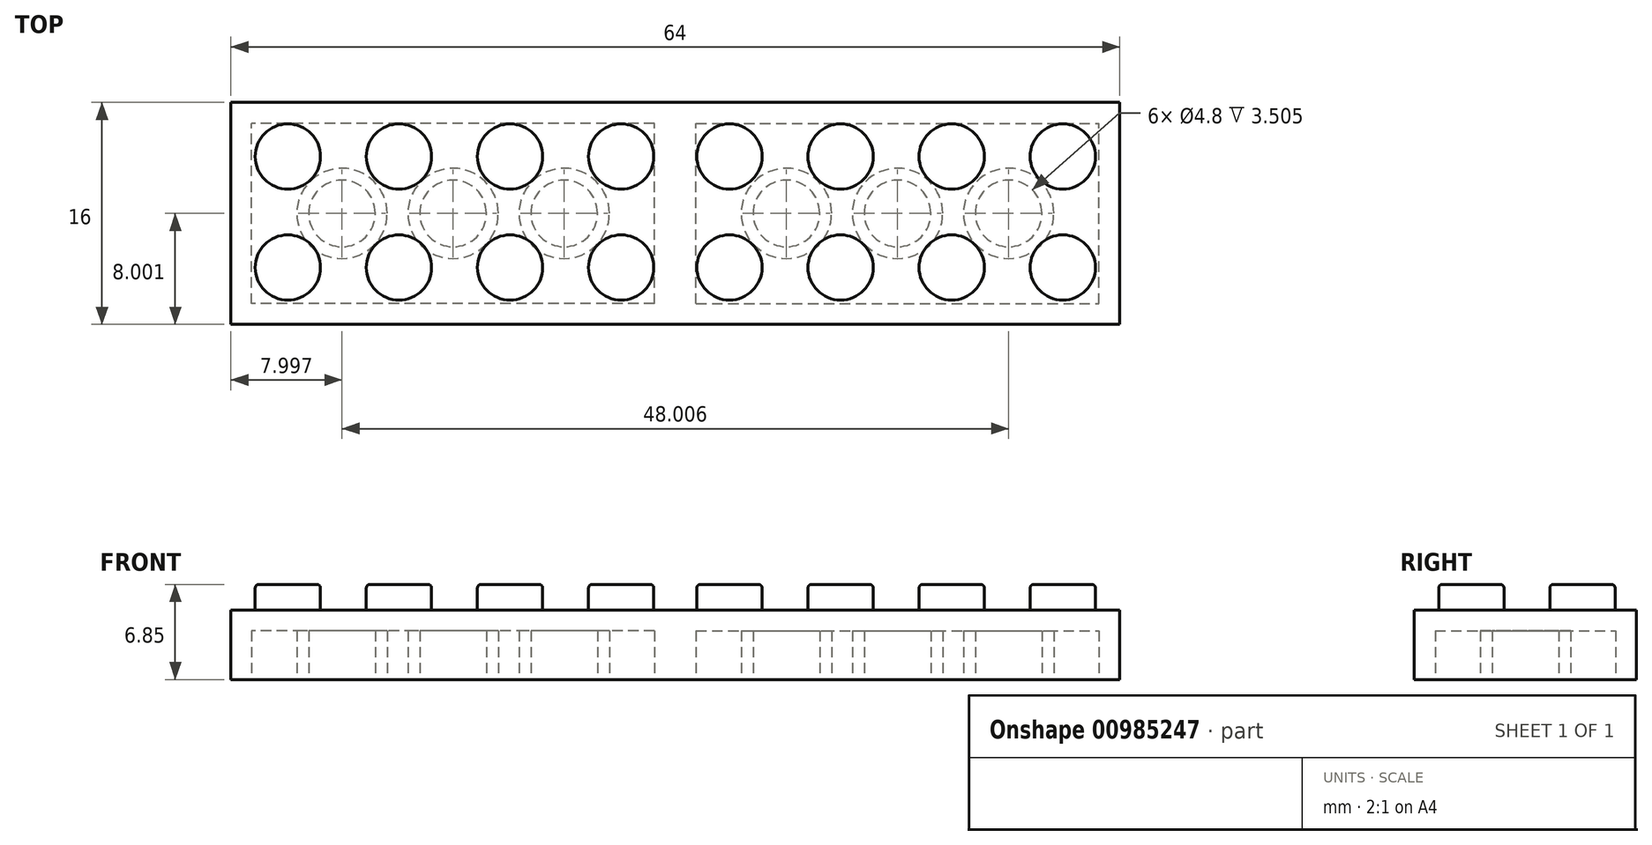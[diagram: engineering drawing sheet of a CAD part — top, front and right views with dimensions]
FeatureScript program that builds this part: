
annotation { "Feature Type Name" : "Feature", "Feature Type Description" : "" }
export const myFeature = defineFeature(function(context is Context, id is Id, definition is map)
    precondition{}
    {
        {
            var Q0;
            Q0=qCreatedBy(makeId("Top.planeOp"),FACE);
            var sketch = newSketch(context, id + "F0", { "sketchPlane" : qUnion([Q0])});
            skLineSegment(sketch, "E0.bottom", {"start": v(0, 0) * mm, "end": v(32, 0) * mm});
            skLineSegment(sketch, "E0.top", {"start": v(0, 16) * mm, "end": v(32, 16) * mm});
            skLineSegment(sketch, "E0.left", {"start": v(0, 0) * mm, "end": v(0, 16) * mm});
            skLineSegment(sketch, "E0.right", {"start": v(32, 0) * mm, "end": v(32, 16) * mm});
            skSolve(sketch);
        }
        {
            var Q0;
            Q0=makeQuery(id+"F0.imprint","IMPRINT",FACE,{"disambiguationData":[TD([[makeQuery(id+"F0.imprint","IMPRINT",EDGE,{"derivedFrom":sQuery(id+"F0.wireOp",EDGE,"E0.bottom")}),1.0]])]});
            extrude(context, id + "F1", {"entities" : qUnion([Q0]), "oppositeDirection" : true, "depth" : 5 * mm, "offsetDistance" : 25.4 * mm});
        }
        {
            var Q0;
            Q0=makeQuery(id+"F1.opExtrude","CAP_FACE",FACE,{"disambiguationData":[OSD([sQuery(id+"F0.wireOp",EDGE,"E0.bottom"),sQuery(id+"F0.wireOp",EDGE,"E0.top"),sQuery(id+"F0.wireOp",EDGE,"E0.left"),sQuery(id+"F0.wireOp",EDGE,"E0.right")])],"isStart":true});
            var sketch = newSketch(context, id + "F2", { "sketchPlane" : qUnion([Q0])});
            skCircle(sketch, "E1", {"center": v(3.9, 12.1) * mm, "radius": 2.35 * mm});
            skCircle(sketch, "E2.0.1.0", {"center": v(3.9, 4.1) * mm, "radius": 2.35 * mm});
            skCircle(sketch, "E2.1.0.0", {"center": v(11.9, 12.1) * mm, "radius": 2.35 * mm});
            skCircle(sketch, "E2.1.1.0", {"center": v(11.9, 4.1) * mm, "radius": 2.35 * mm});
            skCircle(sketch, "E2.2.0.0", {"center": v(19.9, 12.1) * mm, "radius": 2.35 * mm});
            skCircle(sketch, "E2.2.1.0", {"center": v(19.9, 4.1) * mm, "radius": 2.35 * mm});
            skCircle(sketch, "E2.3.0.0", {"center": v(27.9, 12.1) * mm, "radius": 2.35 * mm});
            skCircle(sketch, "E2.3.1.0", {"center": v(27.9, 4.1) * mm, "radius": 2.35 * mm});
            skLineSegment(sketch, "E2.direction1", {"start": v(3.9, 12.1) * mm, "end": v(11.9, 12.1) * mm, "construction": true});
            skLineSegment(sketch, "E2.direction2", {"start": v(3.9, 12.1) * mm, "end": v(3.9, 4.1) * mm, "construction": true});
            skSolve(sketch);
        }
        {
            var Q0;
            Q0=makeQuery(id+"F2.imprint","IMPRINT",FACE,{"disambiguationData":[TD([[makeQuery(id+"F2.imprint","IMPRINT",EDGE,{"derivedFrom":sQuery(id+"F2.wireOp",EDGE,"E1")}),1.0]])]});
            var Q1;
            Q1=makeQuery(id+"F2.imprint","IMPRINT",FACE,{"disambiguationData":[TD([[makeQuery(id+"F2.imprint","IMPRINT",EDGE,{"derivedFrom":sQuery(id+"F2.wireOp",EDGE,"E2.0.1.0")}),1.0]])]});
            var Q2;
            Q2=makeQuery(id+"F2.imprint","IMPRINT",FACE,{"disambiguationData":[TD([[makeQuery(id+"F2.imprint","IMPRINT",EDGE,{"derivedFrom":sQuery(id+"F2.wireOp",EDGE,"E2.1.1.0")}),1.0]])]});
            var Q3;
            Q3=makeQuery(id+"F2.imprint","IMPRINT",FACE,{"disambiguationData":[TD([[makeQuery(id+"F2.imprint","IMPRINT",EDGE,{"derivedFrom":sQuery(id+"F2.wireOp",EDGE,"E2.1.0.0")}),1.0]])]});
            var Q4;
            Q4=makeQuery(id+"F2.imprint","IMPRINT",FACE,{"disambiguationData":[TD([[makeQuery(id+"F2.imprint","IMPRINT",EDGE,{"derivedFrom":sQuery(id+"F2.wireOp",EDGE,"E2.2.0.0")}),1.0]])]});
            var Q5;
            Q5=makeQuery(id+"F2.imprint","IMPRINT",FACE,{"disambiguationData":[TD([[makeQuery(id+"F2.imprint","IMPRINT",EDGE,{"derivedFrom":sQuery(id+"F2.wireOp",EDGE,"E2.2.1.0")}),1.0]])]});
            var Q6;
            Q6=makeQuery(id+"F2.imprint","IMPRINT",FACE,{"disambiguationData":[TD([[makeQuery(id+"F2.imprint","IMPRINT",EDGE,{"derivedFrom":sQuery(id+"F2.wireOp",EDGE,"E2.3.1.0")}),1.0]])]});
            var Q7;
            Q7=makeQuery(id+"F2.imprint","IMPRINT",FACE,{"disambiguationData":[TD([[makeQuery(id+"F2.imprint","IMPRINT",EDGE,{"derivedFrom":sQuery(id+"F2.wireOp",EDGE,"E2.3.0.0")}),1.0]])]});
            extrude(context, id + "F3", {"entities" : qUnion([Q0, Q1, Q2, Q3, Q4, Q5, Q6, Q7]), "operationType" : NewBodyOperationType.ADD, "depth" : 1.85 * mm, "offsetDistance" : 25.4 * mm});
        }
        {
            var Q0;
            Q0=makeQuery(id+"F3.opExtrude","CAP_EDGE",EDGE,{"disambiguationData":[OSD([sQuery(id+"F2.wireOp",EDGE,"E2.0.1.0")])],"isStart":false});
            var Q1;
            Q1=makeQuery(id+"F3.opExtrude","CAP_EDGE",EDGE,{"disambiguationData":[OSD([sQuery(id+"F2.wireOp",EDGE,"E1")])],"isStart":false});
            var Q2;
            Q2=makeQuery(id+"F3.opExtrude","CAP_EDGE",EDGE,{"disambiguationData":[OSD([sQuery(id+"F2.wireOp",EDGE,"E2.1.1.0")])],"isStart":false});
            var Q3;
            Q3=makeQuery(id+"F3.opExtrude","CAP_EDGE",EDGE,{"disambiguationData":[OSD([sQuery(id+"F2.wireOp",EDGE,"E2.1.0.0")])],"isStart":false});
            var Q4;
            Q4=makeQuery(id+"F3.opExtrude","CAP_EDGE",EDGE,{"disambiguationData":[OSD([sQuery(id+"F2.wireOp",EDGE,"E2.2.1.0")])],"isStart":false});
            var Q5;
            Q5=makeQuery(id+"F3.opExtrude","CAP_EDGE",EDGE,{"disambiguationData":[OSD([sQuery(id+"F2.wireOp",EDGE,"E2.2.0.0")])],"isStart":false});
            var Q6;
            Q6=makeQuery(id+"F3.opExtrude","CAP_EDGE",EDGE,{"disambiguationData":[OSD([sQuery(id+"F2.wireOp",EDGE,"E2.3.0.0")])],"isStart":false});
            var Q7;
            Q7=makeQuery(id+"F3.opExtrude","CAP_EDGE",EDGE,{"disambiguationData":[OSD([sQuery(id+"F2.wireOp",EDGE,"E2.3.1.0")])],"isStart":false});
            fillet(context, id + "F4", {"entities" : qUnion([Q0, Q1, Q2, Q3, Q4, Q5, Q6, Q7]), "radius" : 0.25 * mm, "tangentPropagation" : true, "allowEdgeOverflow" : false});
        }
        {
            var Q0;
            Q0=makeQuery(id+"F1.opExtrude","CAP_FACE",FACE,{"disambiguationData":[OSD([sQuery(id+"F0.wireOp",EDGE,"E0.bottom"),sQuery(id+"F0.wireOp",EDGE,"E0.top"),sQuery(id+"F0.wireOp",EDGE,"E0.left"),sQuery(id+"F0.wireOp",EDGE,"E0.right")])],"isStart":false});
            var sketch = newSketch(context, id + "F5", { "sketchPlane" : qUnion([Q0])});
            skLineSegment(sketch, "E3.0", {"start": v(1.5, -1.5) * mm, "end": v(30.5, -1.5) * mm});
            skLineSegment(sketch, "E3.1", {"start": v(1.5, -1.5) * mm, "end": v(1.5, -14.5) * mm});
            skLineSegment(sketch, "E3.2", {"start": v(1.5, -14.5) * mm, "end": v(30.5, -14.5) * mm});
            skLineSegment(sketch, "E3.3", {"start": v(30.5, -1.5) * mm, "end": v(30.5, -14.5) * mm});
            skLineSegment(sketch, "E4.0", {"start": v(-6.35, -22.35) * mm, "end": v(38.35, -22.35) * mm});
            skLineSegment(sketch, "E4.1", {"start": v(-6.35, 6.35) * mm, "end": v(-6.35, -22.35) * mm});
            skLineSegment(sketch, "E4.2", {"start": v(38.35, 6.35) * mm, "end": v(-6.35, 6.35) * mm});
            skLineSegment(sketch, "E4.3", {"start": v(38.35, -22.35) * mm, "end": v(38.35, 6.35) * mm});
            skLineSegment(sketch, "E5", {"start": v(32, -16) * mm, "end": v(0, 0) * mm, "construction": true});
            skLineSegment(sketch, "E6", {"start": v(32, 0) * mm, "end": v(0, -16) * mm, "construction": true});
            skCircle(sketch, "E7", {"center": v(16, -8) * mm, "radius": 3.25 * mm});
            skCircle(sketch, "E8", {"center": v(16, -8) * mm, "radius": 2.4 * mm});
            skCircle(sketch, "E9", {"center": v(24, -8) * mm, "radius": 2.4 * mm});
            skCircle(sketch, "E10", {"center": v(24, -8) * mm, "radius": 3.25 * mm});
            skCircle(sketch, "E11", {"center": v(8, -8) * mm, "radius": 2.4 * mm});
            skCircle(sketch, "E12", {"center": v(8, -8) * mm, "radius": 3.25 * mm});
            skSolve(sketch);
        }
        {
            var Q0;
            Q0=makeQuery(id+"F5.imprint","IMPRINT",FACE,{"disambiguationData":[TD([[makeQuery(id+"F5.imprint","IMPRINT",EDGE,{"derivedFrom":sQuery(id+"F5.wireOp",EDGE,"E3.0")}),-1.0]])]});
            var Q1;
            Q1=makeQuery(id+"F5.imprint","IMPRINT",FACE,{"disambiguationData":[TD([[makeQuery(id+"F5.imprint","IMPRINT",EDGE,{"derivedFrom":sQuery(id+"F5.wireOp",EDGE,"E9")}),1.0]])]});
            var Q2;
            Q2=makeQuery(id+"F5.imprint","IMPRINT",FACE,{"disambiguationData":[TD([[makeQuery(id+"F5.imprint","IMPRINT",EDGE,{"derivedFrom":sQuery(id+"F5.wireOp",EDGE,"E8")}),1.0]])]});
            var Q3;
            Q3=makeQuery(id+"F5.imprint","IMPRINT",FACE,{"disambiguationData":[TD([[makeQuery(id+"F5.imprint","IMPRINT",EDGE,{"derivedFrom":sQuery(id+"F5.wireOp",EDGE,"E11")}),1.0]])]});
            extrude(context, id + "F6", {"entities" : qUnion([Q0, Q1, Q2, Q3]), "operationType" : NewBodyOperationType.REMOVE, "oppositeDirection" : true, "depth" : 3.5 * mm, "offsetDistance" : 25.4 * mm});
        }
        {
            var Q0;
            Q0=makeQuery(id+"F1.opExtrude","SWEPT_BODY",BODY,{"disambiguationData":[OSD([sQuery(id+"F0.wireOp",EDGE,"E0.bottom"),sQuery(id+"F0.wireOp",EDGE,"E0.top"),sQuery(id+"F0.wireOp",EDGE,"E0.left"),sQuery(id+"F0.wireOp",EDGE,"E0.right")])]});
            var Q1;
            Q1=makeQuery(id+"F1.opExtrude","SWEPT_FACE",FACE,{"disambiguationData":[OSD([sQuery(id+"F0.wireOp",EDGE,"E0.left")])]});
            mirror(context, id + "F7", {"operationType" : NewBodyOperationType.ADD, "entities" : qUnion([Q0]), "mirrorPlane" : qUnion([Q1])});
        }
    });
